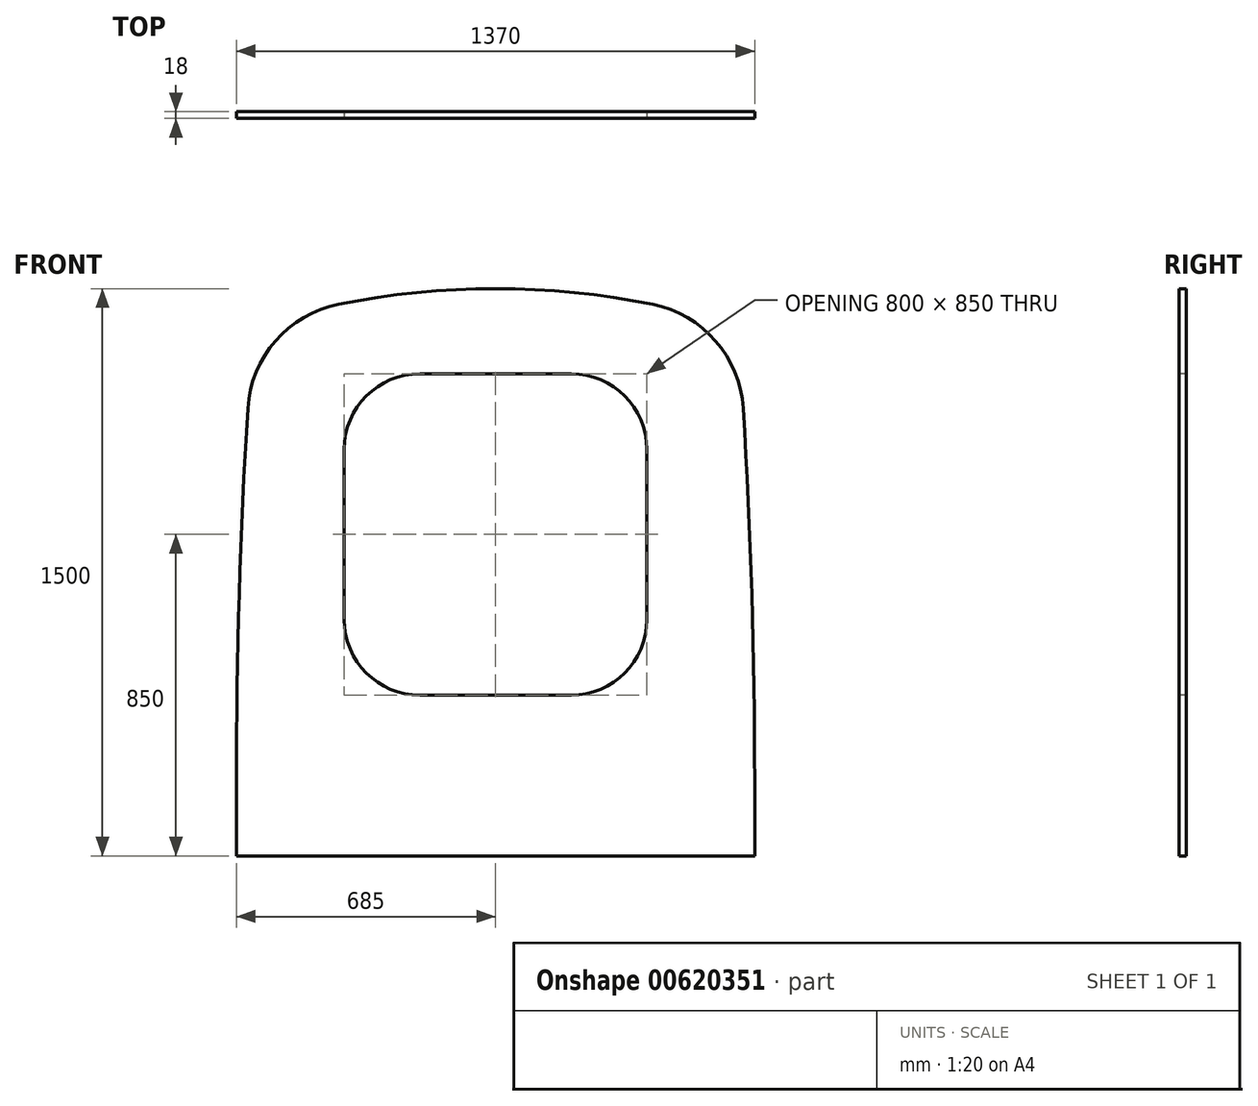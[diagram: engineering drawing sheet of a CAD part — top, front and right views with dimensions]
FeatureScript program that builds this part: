
annotation { "Feature Type Name" : "Feature", "Feature Type Description" : "" }
export const myFeature = defineFeature(function(context is Context, id is Id, definition is map)
    precondition{}
    {
        {
            var Q0;
            Q0=qCreatedBy(makeId("Front.planeOp"),FACE);
            var sketch = newSketch(context, id + "F0", { "sketchPlane" : qUnion([Q0])});
            skLineSegment(sketch, "E0", {"start": v(-685, 0) * mm, "end": v(685, 0) * mm});
            skLineSegment(sketch, "E1", {"start": v(-640, 1400) * mm, "end": v(640, 1400) * mm, "construction": true});
            skArc(sketch, "E2", {"start": v(640, 1400) * mm, "mid": v(0, 1500) * mm, "end": v(-640, 1400) * mm});
            skLineSegment(sketch, "E3", {"start": v(0, 1500) * mm, "end": v(0, 0) * mm, "construction": true});
            skPoint(sketch, "E3.endSnap0", {"position": v(0, 1500) * mm});
            skLineSegment(sketch, "E4", {"start": v(-685, 0) * mm, "end": v(-685, 200) * mm});
            skLineSegment(sketch, "E5", {"start": v(685, 0) * mm, "end": v(685, 200) * mm});
            skLineSegment(sketch, "E6", {"start": v(-685, 200) * mm, "end": v(685, 200) * mm, "construction": true});
            skArc(sketch, "E7", {"start": v(-640, 1400) * mm, "mid": v(-673.75, 800.42) * mm, "end": v(-685, 200) * mm});
            skArc(sketch, "E8", {"start": v(685, 200) * mm, "mid": v(673.75, 800.42) * mm, "end": v(640, 1400) * mm});
            skSolve(sketch);
        }
        {
            var Q0;
            Q0=makeQuery(id+"F0.imprint","IMPRINT",FACE,{"disambiguationData":[TD([[makeQuery(id+"F0.imprint","IMPRINT",EDGE,{"derivedFrom":sQuery(id+"F0.wireOp",EDGE,"E0")}),1.0]])]});
            extrude(context, id + "F1", {"entities" : qUnion([Q0]), "depth" : 18 * mm, "offsetDistance" : 25 * mm});
        }
        {
            var Q0;
            Q0=makeQuery(id+"F1.opExtrude","SWEPT_EDGE",EDGE,{"disambiguationData":[OSD([sQuery(id+"F0.wireOp",EDGE,"E2"),sQuery(id+"F0.wireOp",EDGE,"E7")])]});
            var Q1;
            Q1=makeQuery(id+"F1.opExtrude","SWEPT_EDGE",EDGE,{"disambiguationData":[OSD([sQuery(id+"F0.wireOp",EDGE,"E2"),sQuery(id+"F0.wireOp",EDGE,"E8")])]});
            fillet(context, id + "F2", {"entities" : qUnion([Q0, Q1]), "radius" : 300 * mm, "tangentPropagation" : true, "allowEdgeOverflow" : false});
        }
        {
            var Q0;
            Q0=makeQuery(id+"F1.opExtrude","CAP_FACE",FACE,{"disambiguationData":[OSD([sQuery(id+"F0.wireOp",EDGE,"E0"),sQuery(id+"F0.wireOp",EDGE,"E2"),sQuery(id+"F0.wireOp",EDGE,"E4"),sQuery(id+"F0.wireOp",EDGE,"E5"),sQuery(id+"F0.wireOp",EDGE,"E7"),sQuery(id+"F0.wireOp",EDGE,"E8")])],"isStart":false});
            var sketch = newSketch(context, id + "F3", { "sketchPlane" : qUnion([Q0])});
            skLineSegment(sketch, "E9", {"start": v(0, 0) * mm, "end": v(0, 850) * mm, "construction": true});
            skLineSegment(sketch, "E10.bottom", {"start": v(-400, 1275) * mm, "end": v(400, 1275) * mm});
            skLineSegment(sketch, "E10.top", {"start": v(-400, 425) * mm, "end": v(400, 425) * mm});
            skLineSegment(sketch, "E10.left", {"start": v(-400, 1275) * mm, "end": v(-400, 425) * mm});
            skLineSegment(sketch, "E10.right", {"start": v(400, 1275) * mm, "end": v(400, 425) * mm});
            skPoint(sketch, "E10.middle", {"position": v(0, 850) * mm});
            skSolve(sketch);
        }
        {
            var Q0;
            Q0=makeQuery(id+"F3.imprint","IMPRINT",FACE,{"disambiguationData":[TD([[makeQuery(id+"F3.imprint","IMPRINT",EDGE,{"derivedFrom":sQuery(id+"F3.wireOp",EDGE,"E10.bottom")}),-1.0]])]});
            extrude(context, id + "F4", {"entities" : qUnion([Q0]), "operationType" : NewBodyOperationType.REMOVE, "endBound" : BoundingType.THROUGH_ALL, "oppositeDirection" : true, "depth" : 25 * mm, "offsetDistance" : 25 * mm});
        }
        {
            var Q0;
            Q0=makeQuery(id+"F4.boolean.opBoolean","COPY",EDGE,{"derivedFrom":makeQuery(id+"F4.opExtrude","SWEPT_EDGE",EDGE,{"disambiguationData":[OSD([sQuery(id+"F3.wireOp",EDGE,"E10.top"),sQuery(id+"F3.wireOp",EDGE,"E10.left")])]})});
            var Q1;
            Q1=makeQuery(id+"F4.boolean.opBoolean","COPY",EDGE,{"derivedFrom":makeQuery(id+"F4.opExtrude","SWEPT_EDGE",EDGE,{"disambiguationData":[OSD([sQuery(id+"F3.wireOp",EDGE,"E10.bottom"),sQuery(id+"F3.wireOp",EDGE,"E10.left")])]})});
            var Q2;
            Q2=makeQuery(id+"F4.boolean.opBoolean","COPY",EDGE,{"derivedFrom":makeQuery(id+"F4.opExtrude","SWEPT_EDGE",EDGE,{"disambiguationData":[OSD([sQuery(id+"F3.wireOp",EDGE,"E10.top"),sQuery(id+"F3.wireOp",EDGE,"E10.right")])]})});
            var Q3;
            Q3=makeQuery(id+"F4.boolean.opBoolean","COPY",EDGE,{"derivedFrom":makeQuery(id+"F4.opExtrude","SWEPT_EDGE",EDGE,{"disambiguationData":[OSD([sQuery(id+"F3.wireOp",EDGE,"E10.bottom"),sQuery(id+"F3.wireOp",EDGE,"E10.right")])]})});
            fillet(context, id + "F5", {"entities" : qUnion([Q0, Q1, Q2, Q3]), "radius" : 200 * mm, "tangentPropagation" : true, "allowEdgeOverflow" : false});
        }
    });
